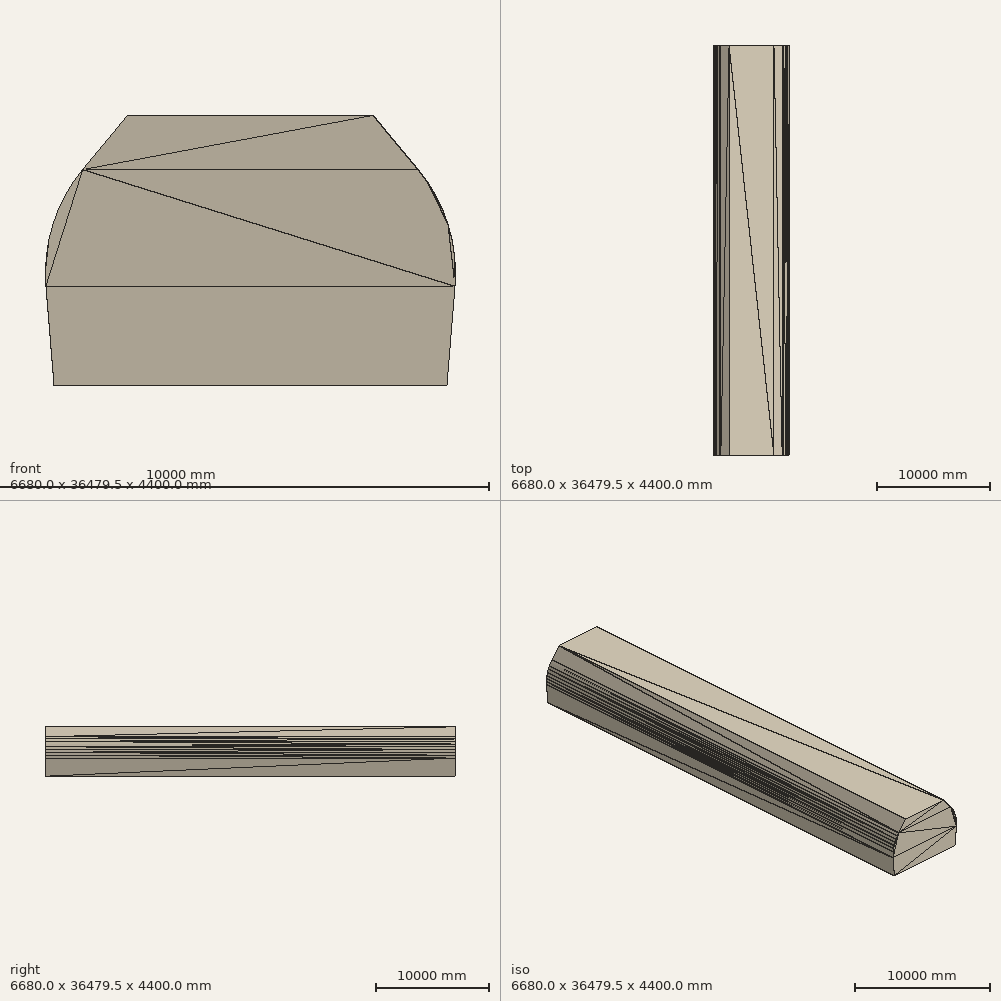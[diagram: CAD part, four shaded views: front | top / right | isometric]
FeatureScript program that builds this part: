
annotation { "Feature Type Name" : "Feature", "Feature Type Description" : "" }
export const myFeature = defineFeature(function(context is Context, id is Id, definition is map)
    precondition{}
    {
        {
            var Q0;
            Q0=qCreatedBy(makeId("Front.planeOp"),FACE);
            var sketch = newSketch(context, id + "F0", { "sketchPlane" : qUnion([Q0])});
            skLineSegment(sketch, "E0", {"start": v(-3200, 0) * mm, "end": v(3200, 0) * mm});
            skLineSegment(sketch, "E1", {"start": v(-1996.44, 4400) * mm, "end": v(1996.44, 4400) * mm});
            skLineSegment(sketch, "E2", {"start": v(0, 1389.38) * mm, "end": v(3043.23, 1389.38) * mm, "construction": true});
            skPoint(sketch, "E3", {"position": v(700, 1829.38) * mm});
            skArc(sketch, "E4", {"start": v(3331.32, 1615.48) * mm, "mid": v(3217.28, 2624.94) * mm, "end": v(2730.5, 3516.6) * mm});
            skLineSegment(sketch, "E5", {"start": v(3200, 0) * mm, "end": v(3331.32, 1615.48) * mm});
            skLineSegment(sketch, "E6", {"start": v(1996.44, 4400) * mm, "end": v(2730.5, 3516.6) * mm});
            skLineSegment(sketch, "E7.MirrorCS", {"start": v(-1996.44, 4400) * mm, "end": v(-2730.5, 3516.6) * mm});
            skArc(sketch, "E8.MirrorCS", {"start": v(-3331.32, 1615.48) * mm, "mid": v(-3217.28, 2624.94) * mm, "end": v(-2730.5, 3516.6) * mm});
            skLineSegment(sketch, "E9.MirrorCS", {"start": v(-3200, 0) * mm, "end": v(-3331.32, 1615.48) * mm});
            skSolve(sketch);
        }
        {
            var Q0;
            Q0=makeQuery(id+"F0.imprint","IMPRINT",FACE,{"disambiguationData":[TD([[makeQuery(id+"F0.imprint","IMPRINT",EDGE,{"derivedFrom":sQuery(id+"F0.wireOp",EDGE,"E0")}),1.0]])]});
            extrude(context, id + "F1", {"entities" : qUnion([Q0]), "oppositeDirection" : true, "depth" : 36479.48 * mm, "offsetDistance" : 25.4 * mm});
        }
    });
